# Revit family: FP-Revit18-OB30SD14PLX1-Oven-0-9000xxxxA
name_source: partatom
category: Specialty Equipment
revit_build: Autodesk Revit 2018 (Build: 20170223_1515(x64)
units: mm (PartAtom-declared; Revit-internal decimal feet)

## family parameters
Always vertical = Yes
Cut with Voids When Loaded = Yes
OmniClass Number = 23.40.40.14.17.11
OmniClass Title = Cookers, Ovens, Stoves
Part Type = Normal
Room Calculation Point = No
Round Connector Dimension = Use Diameter
Shared = No
Work Plane-Based = No

## types (1)
- OB30SD14PLX1
    Cabinet - Height = 693 mm  [stored 2.27362 ft]
    Cavity - Depth = 575 mm
    Cavity - Height = 681 mm  [stored 2.23425 ft]
    Cavity - Width = 724 mm  [stored 2.37533 ft]
    Chassis - Depth = 569 mm  [stored 1.8668 ft]
    Chassis - Height = 675 mm  [stored 2.21457 ft]
    Chassis - Width = 720 mm  [stored 2.3622 ft]
    Connector Note - Electrical = 208-240 V, 60 Hz, 16.6-19.4 A , 3.5-4.6 kW Max Load
    Description = 30" Self Cleaning Oven
    Manufacturer = Fisher & Paykel Appliances
    Material - Body = Fisher & Paykel - Grey
    Material - Buttons and Dials = Fisher & Paykel - Stainless Steel
    Material - Glass = Fisher & Paykel - Glass, Black
    Material - Handle = Fisher & Paykel - Aluminium
    Material - Logo = Fisher & Paykel - Graphics Grey
    Material - Structure = Fisher & Paykel - Black
    Material - Trim = Fisher & Paykel - Stainless Steel
    Model = OB30SD14PLX1
    Product - Depth = 609 mm  [stored 1.99803 ft]
    Product - Height = 690 mm  [stored 2.26378 ft]
    Product - Width = 760 mm  [stored 2.49344 ft]
    URL = www.fisherpaykel.com
    Visibility - Clearance Required = Yes

note: [stored X ft] marks values corroborated as IEEE doubles in the binary element streams (Revit-internal decimal feet)

## geometry (parser evidence)
native form markers: Sweep x2
no freeform markers — native parametric forms only
